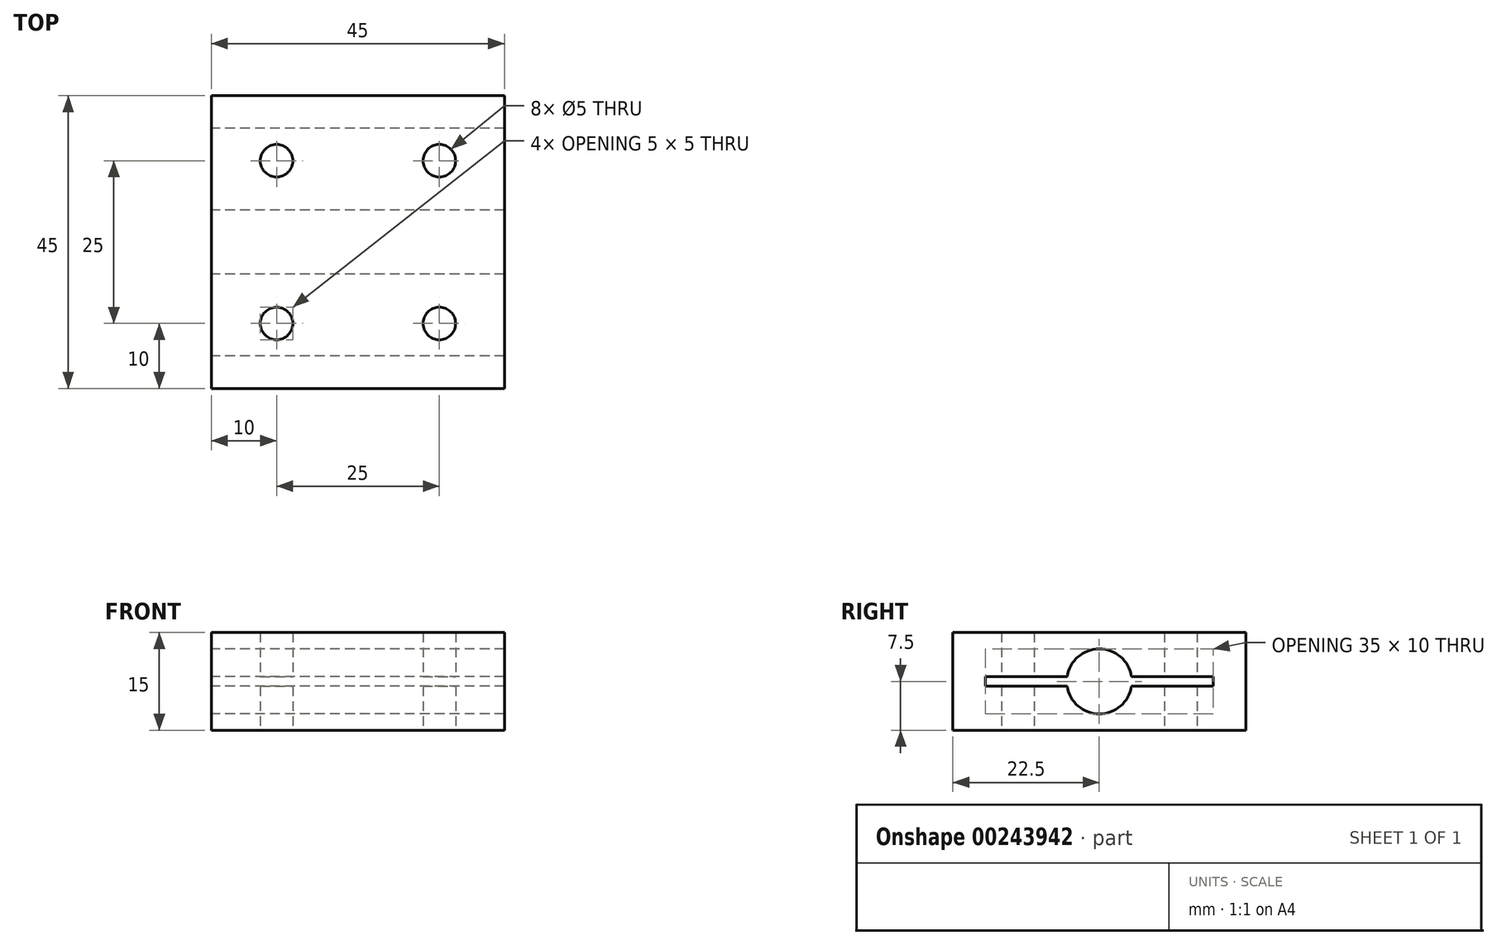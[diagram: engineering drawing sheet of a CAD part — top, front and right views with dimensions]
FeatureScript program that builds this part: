
annotation { "Feature Type Name" : "Feature", "Feature Type Description" : "" }
export const myFeature = defineFeature(function(context is Context, id is Id, definition is map)
    precondition{}
    {
        {
            var Q0;
            Q0=qCreatedBy(makeId("Top.planeOp"),FACE);
            var sketch = newSketch(context, id + "F0", { "sketchPlane" : qUnion([Q0])});
            skLineSegment(sketch, "E0.bottom", {"start": v(0, 0) * mm, "end": v(45, 0) * mm});
            skLineSegment(sketch, "E0.top", {"start": v(0, -45) * mm, "end": v(45, -45) * mm});
            skLineSegment(sketch, "E0.left", {"start": v(0, 0) * mm, "end": v(0, -45) * mm});
            skLineSegment(sketch, "E0.right", {"start": v(45, 0) * mm, "end": v(45, -45) * mm});
            skLineSegment(sketch, "E1.0", {"start": v(10, -10) * mm, "end": v(35, -10) * mm, "construction": true});
            skLineSegment(sketch, "E2.0", {"start": v(10, -35) * mm, "end": v(35, -35) * mm, "construction": true});
            skLineSegment(sketch, "E3.0", {"start": v(10, -10) * mm, "end": v(10, -35) * mm, "construction": true});
            skLineSegment(sketch, "E4.0", {"start": v(35, -10) * mm, "end": v(35, -35) * mm, "construction": true});
            skCircle(sketch, "E5", {"center": v(10, -10) * mm, "radius": 2.5 * mm});
            skCircle(sketch, "E6", {"center": v(35, -10) * mm, "radius": 2.5 * mm});
            skCircle(sketch, "E7", {"center": v(10, -35) * mm, "radius": 2.5 * mm});
            skCircle(sketch, "E8", {"center": v(35, -35) * mm, "radius": 2.5 * mm});
            skSolve(sketch);
        }
        {
            var Q0;
            Q0=makeQuery(id+"F0.imprint","IMPRINT",FACE,{"disambiguationData":[TD([[makeQuery(id+"F0.imprint","IMPRINT",EDGE,{"derivedFrom":sQuery(id+"F0.wireOp",EDGE,"E0.bottom")}),-1.0]])]});
            extrude(context, id + "F1", {"entities" : qUnion([Q0]), "depth" : 15 * mm, "offsetDistance" : 25 * mm});
        }
        {
            var Q0;
            Q0=qCreatedBy(makeId("Right.planeOp"),FACE);
            var sketch = newSketch(context, id + "F2", { "sketchPlane" : qUnion([Q0])});
            skLineSegment(sketch, "E9", {"start": v(0, 0) * mm, "end": v(0, 7.5) * mm, "construction": true});
            skLineSegment(sketch, "E10", {"start": v(0, 7.5) * mm, "end": v(-45, 7.5) * mm, "construction": true});
            skLineSegment(sketch, "E11", {"start": v(0, 0) * mm, "end": v(-22.5, 0) * mm, "construction": true});
            skLineSegment(sketch, "E12", {"start": v(-22.5, 0) * mm, "end": v(-22.5, 7.5) * mm, "construction": true});
            skLineSegment(sketch, "E13.0", {"start": v(-5, 6.75) * mm, "end": v(-5, 8.25) * mm});
            skLineSegment(sketch, "E14.0", {"start": v(-40, 6.75) * mm, "end": v(-40, 8.25) * mm});
            skLineSegment(sketch, "E15.0", {"start": v(-5, 8.25) * mm, "end": v(-17.56, 8.25) * mm});
            skLineSegment(sketch, "E16.0", {"start": v(-5, 6.75) * mm, "end": v(-17.56, 6.75) * mm});
            skArc(sketch, "E17", {"start": v(-27.44, 6.75) * mm, "mid": v(-22.5, 2.5) * mm, "end": v(-17.56, 6.75) * mm});
            skLineSegment(sketch, "E18.trimOffspring", {"start": v(-27.44, 8.25) * mm, "end": v(-40, 8.25) * mm});
            skLineSegment(sketch, "E19.trimOffspring", {"start": v(-27.44, 6.75) * mm, "end": v(-40, 6.75) * mm});
            skArc(sketch, "E20.trimOffspring", {"start": v(-17.56, 8.25) * mm, "mid": v(-22.5, 12.5) * mm, "end": v(-27.44, 8.25) * mm});
            skSolve(sketch);
        }
        {
            var Q0;
            Q0=makeQuery(id+"F2.imprint","IMPRINT",FACE,{"disambiguationData":[TD([[makeQuery(id+"F2.imprint","IMPRINT",EDGE,{"derivedFrom":sQuery(id+"F2.wireOp",EDGE,"E13.0")}),1.0]])]});
            extrude(context, id + "F3", {"entities" : qUnion([Q0]), "operationType" : NewBodyOperationType.REMOVE, "depth" : 50 * mm, "offsetDistance" : 25 * mm});
        }
    });
